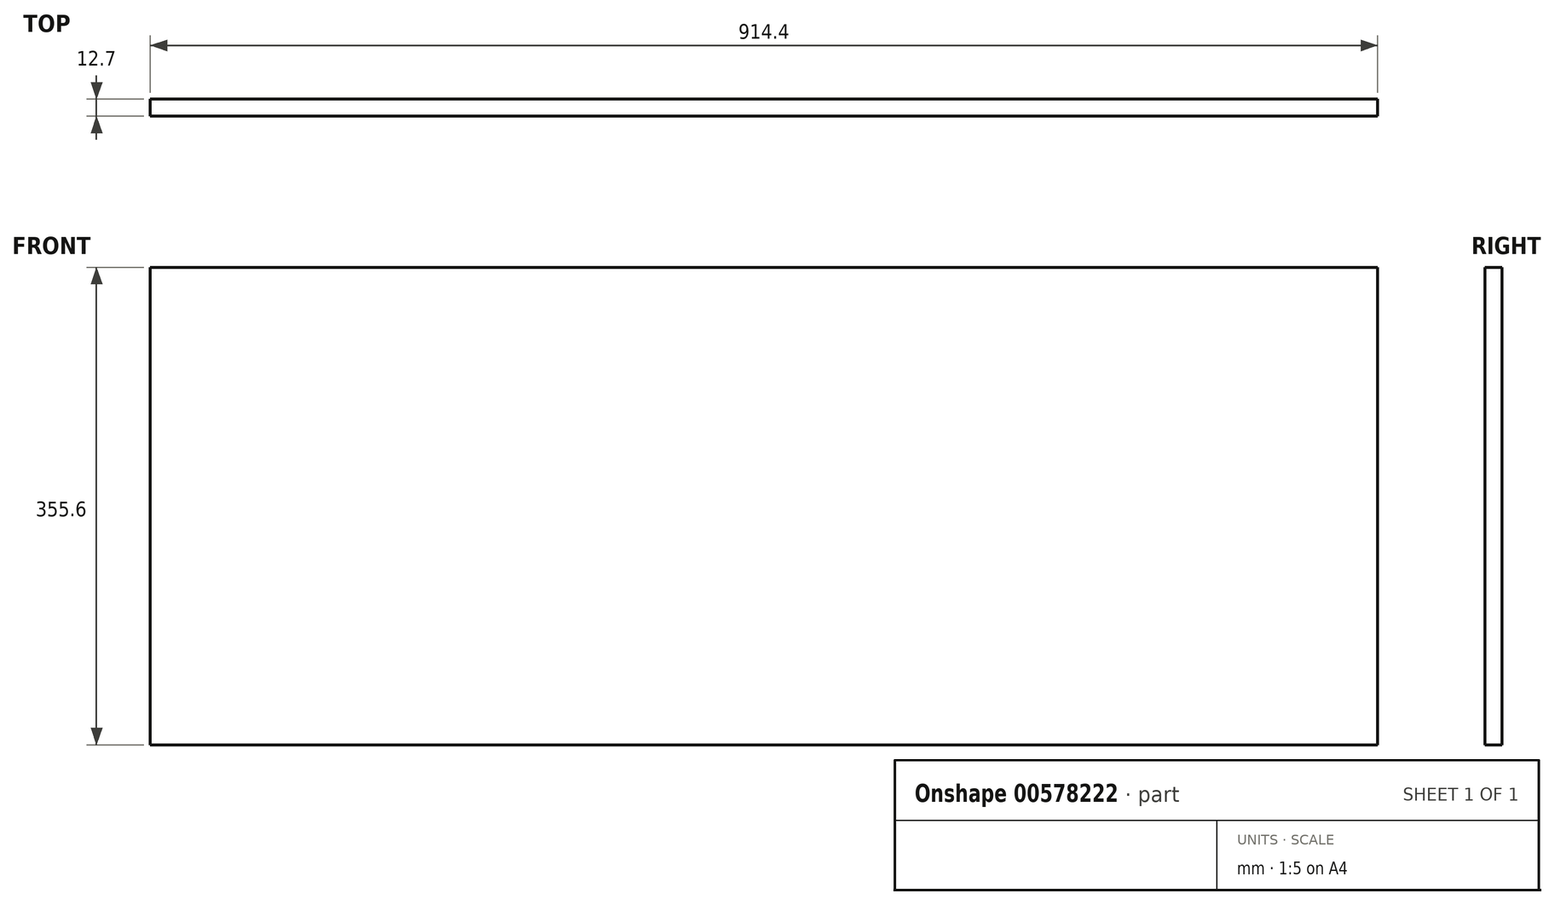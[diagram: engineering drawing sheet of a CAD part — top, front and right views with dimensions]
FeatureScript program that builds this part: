
annotation { "Feature Type Name" : "Feature", "Feature Type Description" : "" }
export const myFeature = defineFeature(function(context is Context, id is Id, definition is map)
    precondition{}
    {
        {
            var Q0;
            Q0=qCreatedBy(makeId("Front.planeOp"),FACE);
            var sketch = newSketch(context, id + "F0", { "sketchPlane" : qUnion([Q0])});
            skLineSegment(sketch, "E0.bottom", {"start": v(-458.47, 189.01) * mm, "end": v(455.93, 189.01) * mm});
            skLineSegment(sketch, "E0.top", {"start": v(-458.47, -166.59) * mm, "end": v(455.93, -166.59) * mm});
            skLineSegment(sketch, "E0.left", {"start": v(-458.47, 189.01) * mm, "end": v(-458.47, -166.59) * mm});
            skLineSegment(sketch, "E0.right", {"start": v(455.93, 189.01) * mm, "end": v(455.93, -166.59) * mm});
            skSolve(sketch);
        }
        {
            var Q0;
            Q0 = qSketchRegion(id + "F0", true);
            extrude(context, id + "F1", {"entities" : qUnion([Q0]), "depth" : 12.7 * mm, "offsetDistance" : 25.4 * mm});
        }
    });
